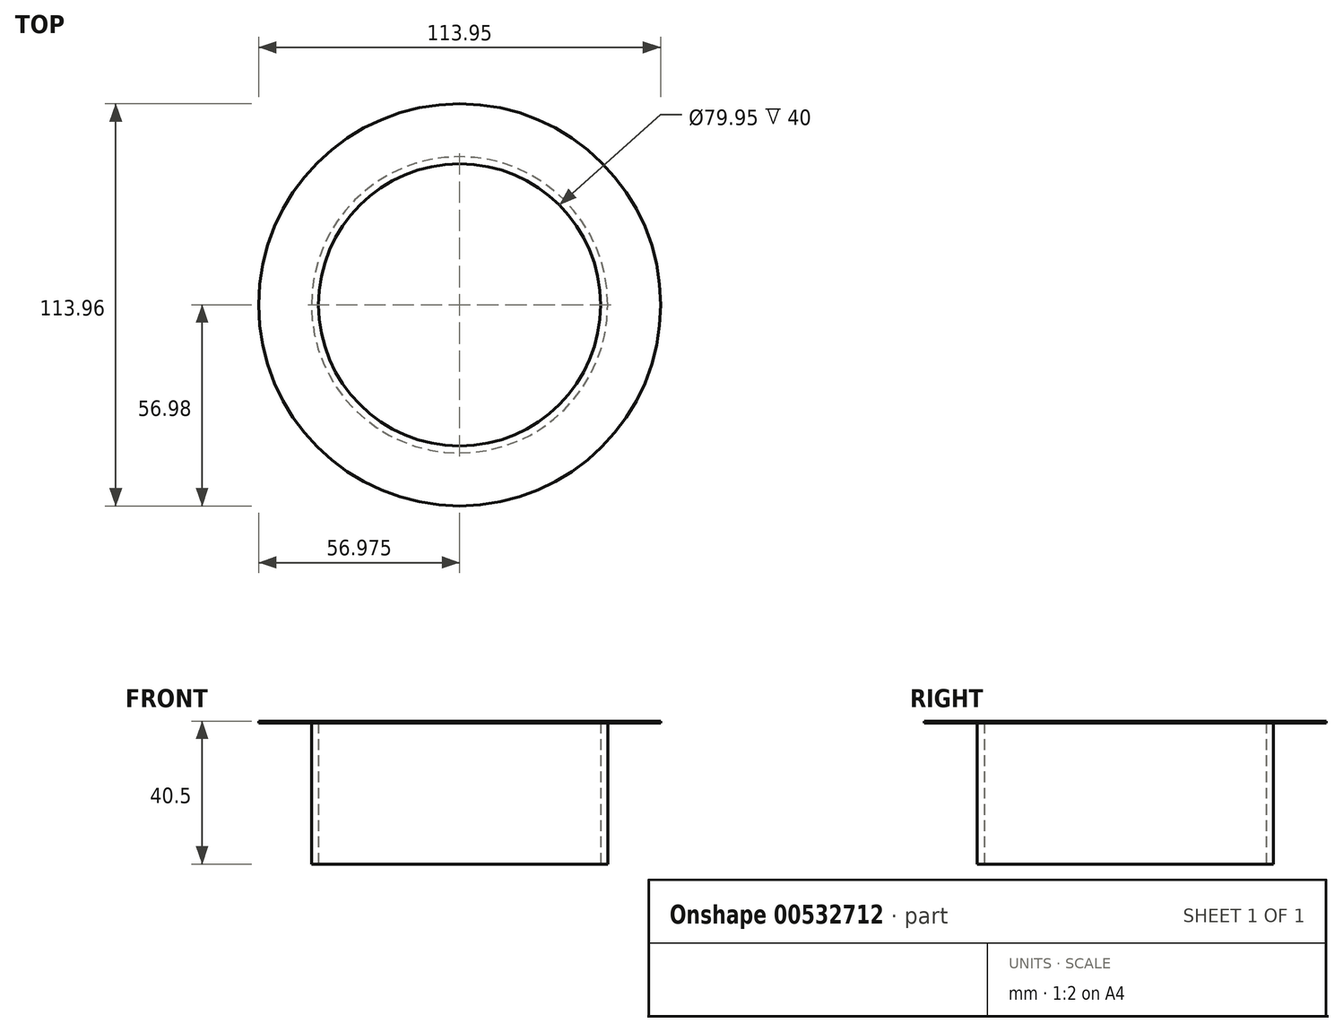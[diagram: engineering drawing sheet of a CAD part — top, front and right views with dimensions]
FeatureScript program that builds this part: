
annotation { "Feature Type Name" : "Feature", "Feature Type Description" : "" }
export const myFeature = defineFeature(function(context is Context, id is Id, definition is map)
    precondition{}
    {
        {
            var Q0;
            Q0=qCreatedBy(makeId("Front.planeOp"),FACE);
            var sketch = newSketch(context, id + "F0", { "sketchPlane" : qUnion([Q0])});
            skLineSegment(sketch, "E0", {"start": v(-41.4, 44.65) * mm, "end": v(-41.4, 44.15) * mm});
            skLineSegment(sketch, "E1", {"start": v(-41.4, 44.15) * mm, "end": v(-26.5, 44.15) * mm});
            skLineSegment(sketch, "E2", {"start": v(-26.4, 44.05) * mm, "end": v(-26.4, 4.15) * mm});
            skLineSegment(sketch, "E3", {"start": v(-26.4, 4.15) * mm, "end": v(-24.4, 4.15) * mm});
            skLineSegment(sketch, "E4", {"start": v(-24.4, 4.15) * mm, "end": v(-24.4, 44.15) * mm});
            skLineSegment(sketch, "E5", {"start": v(-24.9, 44.65) * mm, "end": v(-41.4, 44.65) * mm});
            skPoint(sketch, "E6.visualSharp", {"position": v(-24.4, 44.65) * mm});
            skArc(sketch, "E6.filletArc", {"start": v(-24.4, 44.15) * mm, "mid": v(-24.54, 44.5) * mm, "end": v(-24.9, 44.65) * mm});
            skPoint(sketch, "E7.visualSharp", {"position": v(-26.4, 44.15) * mm});
            skArc(sketch, "E7.filletArc", {"start": v(-26.4, 44.05) * mm, "mid": v(-26.43, 44.12) * mm, "end": v(-26.5, 44.15) * mm});
            skLineSegment(sketch, "E8", {"start": v(15.57, 4.15) * mm, "end": v(15.57, 30.47) * mm});
            skSolve(sketch);
        }
        {
            var Q0;
            Q0 = qSketchRegion(id + "F0", true);
            var Q1;
            Q1=sQuery(id+"F0.wireOp",EDGE,"E8");
            revolve(context, id + "F1", {"entities" : qUnion([Q0]), "axis" : qUnion([Q1]), "revolveType" : RevolveType.FULL});
        }
    });
